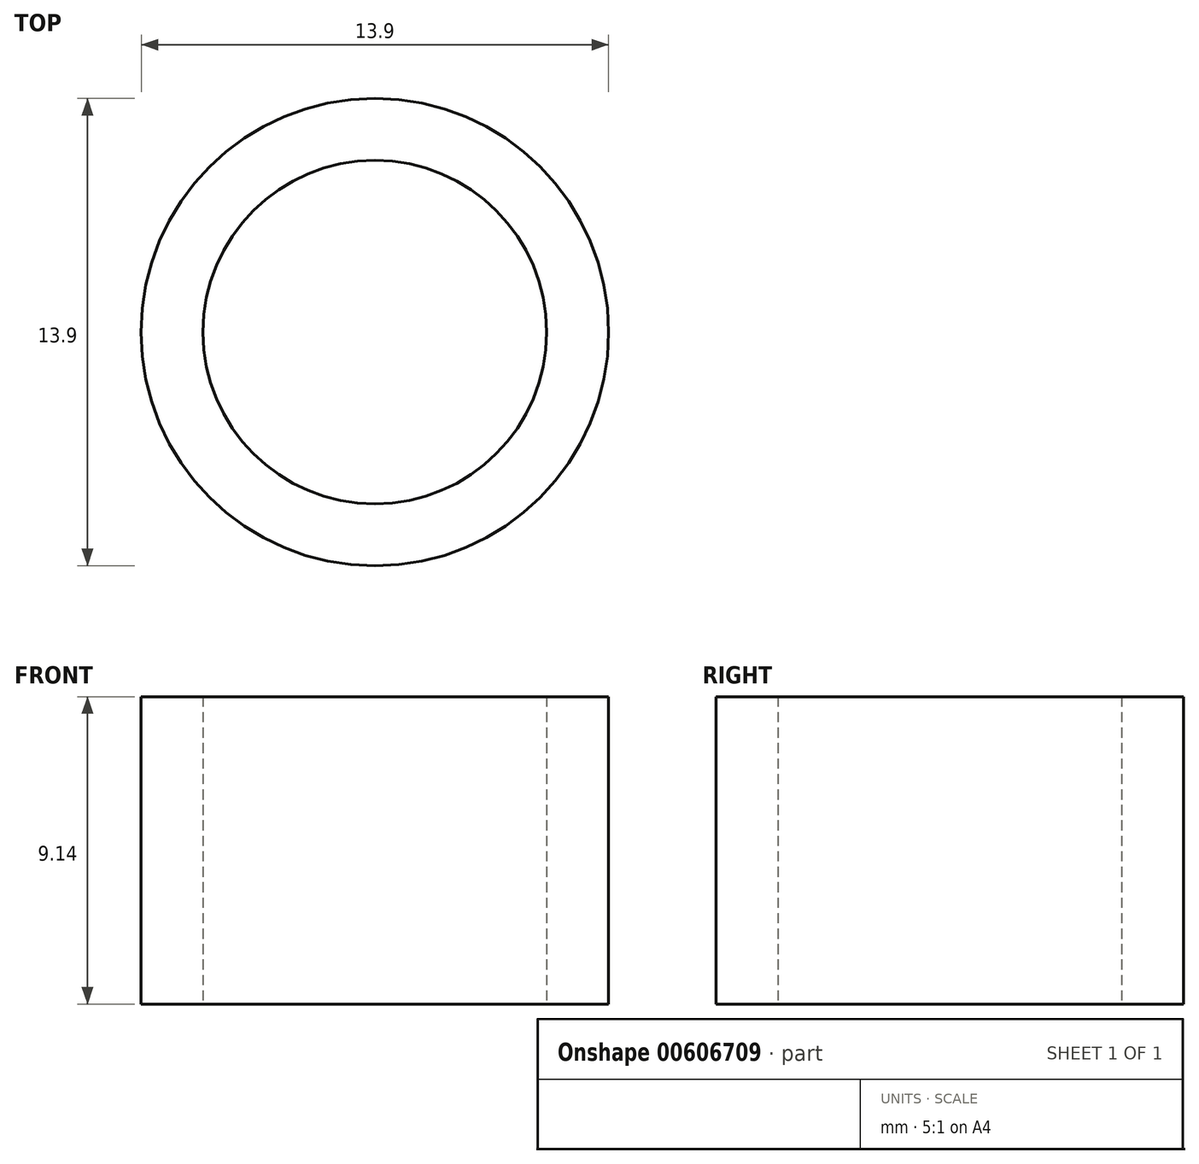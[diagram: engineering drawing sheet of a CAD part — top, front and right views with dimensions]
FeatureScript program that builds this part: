
annotation { "Feature Type Name" : "Feature", "Feature Type Description" : "" }
export const myFeature = defineFeature(function(context is Context, id is Id, definition is map)
    precondition{}
    {
        {
            var Q0;
            Q0=qCreatedBy(makeId("Top.planeOp"),FACE);
            var sketch = newSketch(context, id + "F0", { "sketchPlane" : qUnion([Q0])});
            skCircle(sketch, "E0", {"center": v(0, 0) * mm, "radius": 6.95 * mm});
            skCircle(sketch, "E1", {"center": v(0, 0) * mm, "radius": 5.11 * mm});
            skSolve(sketch);
        }
        {
            var Q0;
            Q0 = qSketchRegion(id + "F0", true);
            extrude(context, id + "F1", {"entities" : qUnion([Q0]), "depth" : 9.14 * mm, "offsetDistance" : 25.4 * mm});
        }
    });
